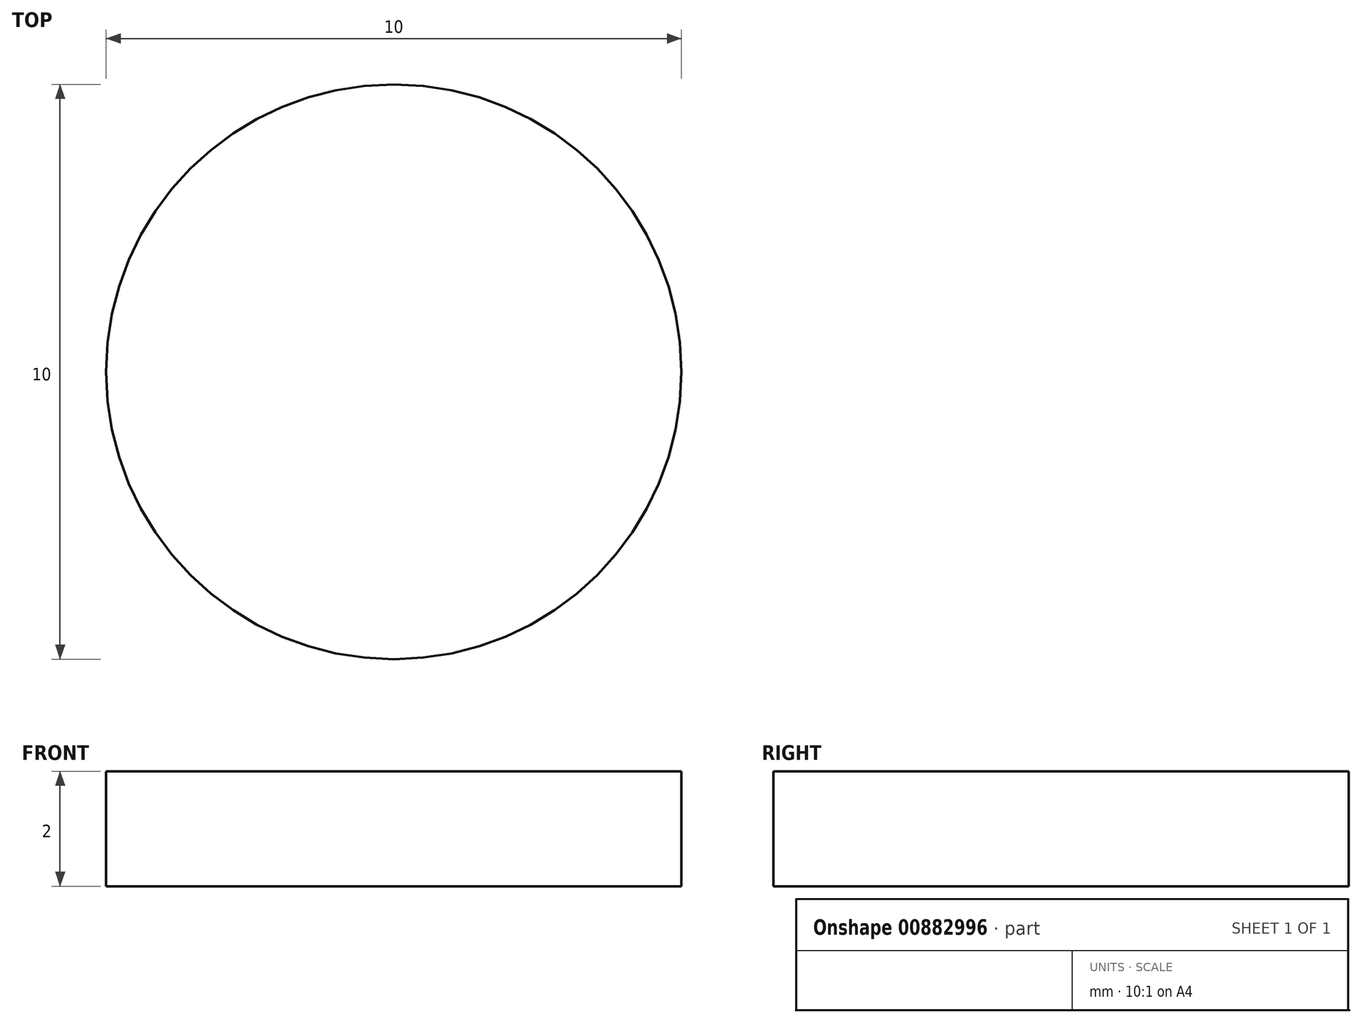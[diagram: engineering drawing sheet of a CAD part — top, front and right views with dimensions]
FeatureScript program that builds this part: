
annotation { "Feature Type Name" : "Feature", "Feature Type Description" : "" }
export const myFeature = defineFeature(function(context is Context, id is Id, definition is map)
    precondition{}
    {
        {
            var Q0;
            Q0=qCreatedBy(makeId("Top.planeOp"),FACE);
            var sketch = newSketch(context, id + "F0", { "sketchPlane" : qUnion([Q0])});
            skCircle(sketch, "E0", {"center": v(0, 0) * mm, "radius": 5 * mm});
            skSolve(sketch);
        }
        {
            var Q0;
            Q0 = qSketchRegion(id + "F0", true);
            extrude(context, id + "F1", {"entities" : qUnion([Q0]), "depth" : 2 * mm, "offsetDistance" : 25 * mm});
        }
    });
